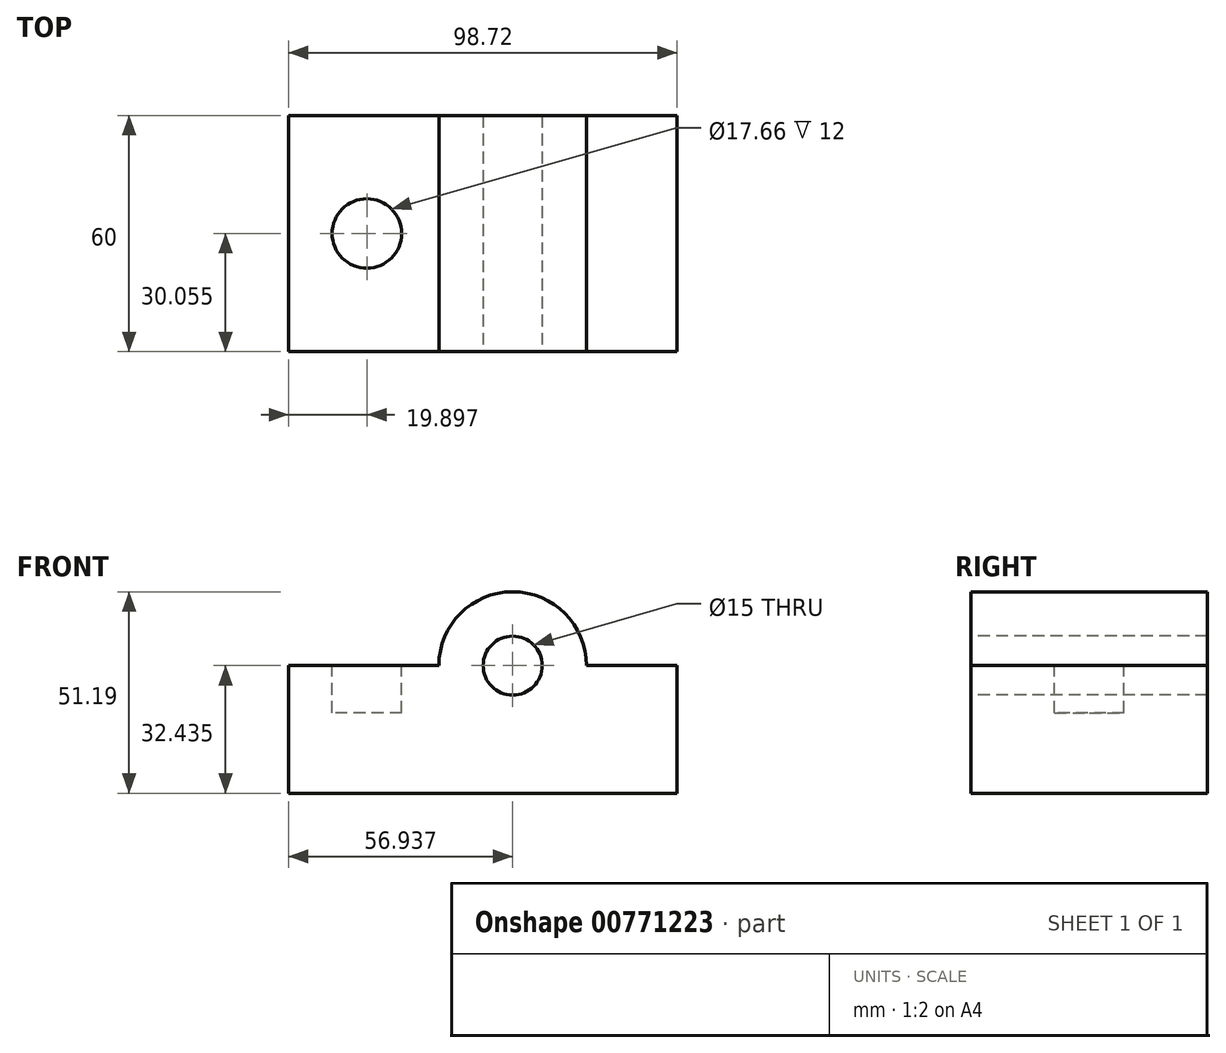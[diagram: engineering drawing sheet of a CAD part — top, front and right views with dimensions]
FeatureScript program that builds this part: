
annotation { "Feature Type Name" : "Feature", "Feature Type Description" : "" }
export const myFeature = defineFeature(function(context is Context, id is Id, definition is map)
    precondition{}
    {
        {
            var Q0;
            Q0=qCreatedBy(makeId("Front.planeOp"),FACE);
            var sketch = newSketch(context, id + "F0", { "sketchPlane" : qUnion([Q0])});
            skLineSegment(sketch, "E0", {"start": v(0, 0) * mm, "end": v(0, 32.43) * mm});
            skLineSegment(sketch, "E1", {"start": v(0, 32.43) * mm, "end": v(-22.52, 32.43) * mm});
            skLineSegment(sketch, "E2", {"start": v(0, 0) * mm, "end": v(-98.72, 0) * mm});
            skLineSegment(sketch, "E3", {"start": v(-98.72, 0) * mm, "end": v(-98.72, 32.43) * mm});
            skLineSegment(sketch, "E4", {"start": v(-98.72, 32.43) * mm, "end": v(-61.61, 32.43) * mm});
            skArc(sketch, "E5", {"start": v(-23.02, 32.43) * mm, "mid": v(-41.78, 51.2) * mm, "end": v(-60.54, 32.43) * mm});
            skLineSegment(sketch, "E6", {"start": v(-61.61, 32.43) * mm, "end": v(-60.54, 32.43) * mm});
            skLineSegment(sketch, "E7.trimOffspring", {"start": v(-23.02, 32.43) * mm, "end": v(-22.52, 32.43) * mm});
            skSolve(sketch);
        }
        {
            var Q0;
            Q0 = qSketchRegion(id + "F0", true);
            extrude(context, id + "F1", {"entities" : qUnion([Q0]), "depth" : 60 * mm, "offsetDistance" : 25 * mm});
        }
        {
            var Q0;
            Q0=makeQuery(id+"F1.opExtrude","CAP_FACE",FACE,{"disambiguationData":[OSD([sQuery(id+"F0.wireOp",EDGE,"E0"),sQuery(id+"F0.wireOp",EDGE,"E1"),sQuery(id+"F0.wireOp",EDGE,"E2"),sQuery(id+"F0.wireOp",EDGE,"E3"),sQuery(id+"F0.wireOp",EDGE,"E4"),sQuery(id+"F0.wireOp",EDGE,"E5"),sQuery(id+"F0.wireOp",EDGE,"E6"),sQuery(id+"F0.wireOp",EDGE,"E7.trimOffspring")])],"isStart":false});
            var sketch = newSketch(context, id + "F2", { "sketchPlane" : qUnion([Q0])});
            skCircle(sketch, "E8", {"center": v(-41.78, 32.43) * mm, "radius": 7.5 * mm});
            skSolve(sketch);
        }
        {
            var Q0;
            Q0 = qSketchRegion(id + "F2", true);
            extrude(context, id + "F3", {"entities" : qUnion([Q0]), "operationType" : NewBodyOperationType.REMOVE, "endBound" : BoundingType.UP_TO_NEXT, "oppositeDirection" : true, "depth" : 25 * mm, "offsetDistance" : 25 * mm});
        }
        {
            var Q0;
            Q0=makeQuery(id+"F1.opExtrude","SWEPT_FACE",FACE,{"disambiguationData":[OSD([sQuery(id+"F0.wireOp",EDGE,"E4"),sQuery(id+"F0.wireOp",EDGE,"E6")])]});
            var sketch = newSketch(context, id + "F4", { "sketchPlane" : qUnion([Q0])});
            skSolve(sketch);
        }
        {
            var Q0;
            {var subQ0=sQuery(id+"F0.wireOp",EDGE,"E4");Q0=makeQuery(id+"F4.imprint","IMPRINT",FACE,{"disambiguationData":[TD([[makeQuery(id+"F4.imprint","IMPRINT",EDGE,{"derivedFrom":makeQuery(id+"F1.opExtrude","SWEPT_EDGE",EDGE,{"disambiguationData":[OSD([sQuery(id+"F0.wireOp",EDGE,"E3"),subQ0])]})}),-1.0]])]});}
            var sketch = newSketch(context, id + "F5", { "sketchPlane" : qUnion([Q0])});
            skCircle(sketch, "E9", {"center": v(-78.82, -29.94) * mm, "radius": 8.83 * mm});
            skSolve(sketch);
        }
        {
            var Q0;
            Q0 = qSketchRegion(id + "F5", true);
            extrude(context, id + "F6", {"entities" : qUnion([Q0]), "operationType" : NewBodyOperationType.REMOVE, "oppositeDirection" : true, "depth" : 12 * mm, "offsetDistance" : 25 * mm});
        }
    });
